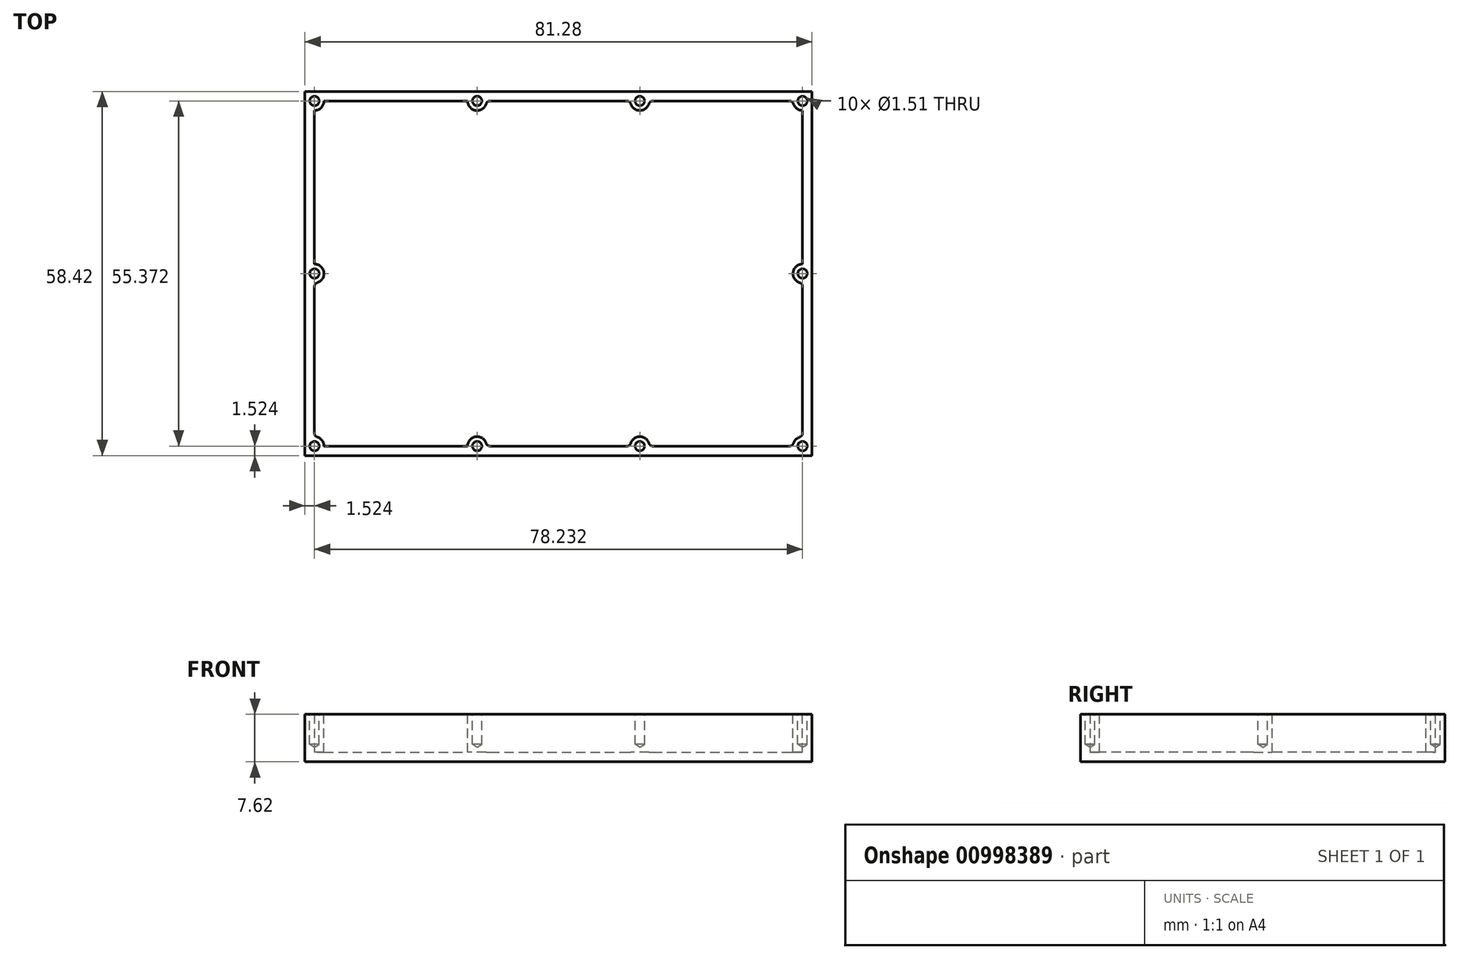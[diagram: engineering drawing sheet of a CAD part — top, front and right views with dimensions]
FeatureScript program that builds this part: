
annotation { "Feature Type Name" : "Feature", "Feature Type Description" : "" }
export const myFeature = defineFeature(function(context is Context, id is Id, definition is map)
    precondition{}
    {
        {
            var Q0;
            Q0=qCreatedBy(makeId("Top.planeOp"),FACE);
            var sketch = newSketch(context, id + "F0", { "sketchPlane" : qUnion([Q0])});
            skLineSegment(sketch, "E0.bottom", {"start": v(-40.64, 29.21) * mm, "end": v(40.64, 29.21) * mm});
            skLineSegment(sketch, "E0.top", {"start": v(-40.64, -29.2) * mm, "end": v(40.64, -29.2) * mm});
            skLineSegment(sketch, "E0.left", {"start": v(-40.64, 29.21) * mm, "end": v(-40.64, -29.2) * mm});
            skLineSegment(sketch, "E0.right", {"start": v(40.64, 29.2) * mm, "end": v(40.64, -29.2) * mm});
            skLineSegment(sketch, "E1", {"start": v(-40.64, -29.2) * mm, "end": v(40.64, 29.2) * mm, "construction": true});
            skSolve(sketch);
        }
        {
            var Q0;
            Q0 = qSketchRegion(id + "F0", true);
            extrude(context, id + "F1", {"entities" : qUnion([Q0]), "endBound" : BoundingType.SYMMETRIC, "depth" : 7.62 * mm, "offsetDistance" : 25.4 * mm});
        }
        {
            var Q0;
            Q0=makeQuery(id+"F1.opExtrude","CAP_FACE",FACE,{"disambiguationData":[OSD([sQuery(id+"F0.wireOp",EDGE,"E0.bottom"),sQuery(id+"F0.wireOp",EDGE,"E0.top"),sQuery(id+"F0.wireOp",EDGE,"E0.left"),sQuery(id+"F0.wireOp",EDGE,"E0.right")])],"isStart":false});
            shell(context, id + "F2", {"entities" : qUnion([Q0]), "thickness" : 1.52 * mm});
        }
        {
            var Q0;
            Q0=makeQuery(id+"F1.opExtrude","CAP_FACE",FACE,{"disambiguationData":[OSD([sQuery(id+"F0.wireOp",EDGE,"E0.bottom"),sQuery(id+"F0.wireOp",EDGE,"E0.top"),sQuery(id+"F0.wireOp",EDGE,"E0.left"),sQuery(id+"F0.wireOp",EDGE,"E0.right")])],"isStart":false});
            var sketch = newSketch(context, id + "F3", { "sketchPlane" : qUnion([Q0])});
            skPoint(sketch, "E2", {"position": v(-39.12, 27.69) * mm});
            skPoint(sketch, "E3.1.0.0", {"position": v(-13.04, 27.69) * mm});
            skPoint(sketch, "E3.2.0.0", {"position": v(13.04, 27.69) * mm});
            skPoint(sketch, "E3.3.0.0", {"position": v(39.12, 27.69) * mm});
            skLineSegment(sketch, "E3.direction1", {"start": v(-39.12, 27.69) * mm, "end": v(-13.04, 27.69) * mm, "construction": true});
            skPoint(sketch, "E4.1.0.0", {"position": v(-39.12, 0) * mm});
            skPoint(sketch, "E4.2.0.0", {"position": v(-39.12, -27.69) * mm});
            skLineSegment(sketch, "E4.direction1", {"start": v(-39.12, 27.69) * mm, "end": v(-39.12, 0) * mm, "construction": true});
            skPoint(sketch, "E5.1.0.0", {"position": v(39.12, 0) * mm});
            skPoint(sketch, "E5.2.0.0", {"position": v(39.12, -27.69) * mm});
            skLineSegment(sketch, "E5.direction1", {"start": v(39.12, 27.69) * mm, "end": v(39.12, 0) * mm, "construction": true});
            skPoint(sketch, "E6.1.0.0", {"position": v(-13.04, -27.69) * mm});
            skPoint(sketch, "E6.2.0.0", {"position": v(13.04, -27.69) * mm});
            skLineSegment(sketch, "E6.direction1", {"start": v(-39.12, -27.69) * mm, "end": v(-13.04, -27.69) * mm, "construction": true});
            skCircle(sketch, "E7", {"center": v(-39.12, 27.69) * mm, "radius": 1.52 * mm});
            skCircle(sketch, "E8", {"center": v(-13.04, 27.69) * mm, "radius": 1.52 * mm});
            skCircle(sketch, "E9", {"center": v(13.04, 27.69) * mm, "radius": 1.52 * mm});
            skCircle(sketch, "E10", {"center": v(39.12, 27.69) * mm, "radius": 1.52 * mm});
            skCircle(sketch, "E11", {"center": v(39.12, 0) * mm, "radius": 1.52 * mm});
            skCircle(sketch, "E12", {"center": v(-39.12, 0) * mm, "radius": 1.52 * mm});
            skCircle(sketch, "E13", {"center": v(-39.12, -27.69) * mm, "radius": 1.52 * mm});
            skCircle(sketch, "E14", {"center": v(-13.04, -27.69) * mm, "radius": 1.52 * mm});
            skCircle(sketch, "E15", {"center": v(13.04, -27.69) * mm, "radius": 1.52 * mm});
            skCircle(sketch, "E16", {"center": v(39.12, -27.69) * mm, "radius": 1.52 * mm});
            skSolve(sketch);
        }
        {
            var Q0;
            {var subQ0=sQuery(id+"F3.wireOp",EDGE,"E7");var subQ1=sQuery(id+"F0.wireOp",EDGE,"E0.bottom");var subQ2=makeQuery(id+"F2.opShell","OFFSET_EDGE",EDGE,{"disambiguationData":[OSD([subQ1]),TDD([makeQuery(id+"F1.opExtrude","CAP_EDGE",EDGE,{"disambiguationData":[OSD([subQ1])],"isStart":false})])]});var subQ3=makeQuery(id+"F3.imprint","INTERSECT",VERTEX,{"derivedFrom":[subQ2,subQ0]});Q0=makeQuery(id+"F3.imprint","IMPRINT",FACE,{"disambiguationData":[TD([[makeQuery(id+"F3.imprint","IMPRINT",EDGE,{"disambiguationData":[TD([[subQ3,1.0]])],"derivedFrom":subQ0}),1.0]])]});}
            var Q1;
            {var subQ0=sQuery(id+"F3.wireOp",EDGE,"E8");var subQ1=sQuery(id+"F0.wireOp",EDGE,"E0.bottom");var subQ2=makeQuery(id+"F2.opShell","OFFSET_EDGE",EDGE,{"disambiguationData":[OSD([subQ1]),TDD([makeQuery(id+"F1.opExtrude","CAP_EDGE",EDGE,{"disambiguationData":[OSD([subQ1])],"isStart":false})])]});var subQ3=makeQuery(id+"F3.imprint","INTERSECT",VERTEX,{"disambiguationData":[OD(0.0)],"derivedFrom":[subQ2,subQ0]});Q1=makeQuery(id+"F3.imprint","IMPRINT",FACE,{"disambiguationData":[TD([[makeQuery(id+"F3.imprint","IMPRINT",EDGE,{"disambiguationData":[TD([[subQ3,1.0]])],"derivedFrom":subQ0}),1.0]])]});}
            var Q2;
            {var subQ0=sQuery(id+"F3.wireOp",EDGE,"E9");var subQ1=sQuery(id+"F0.wireOp",EDGE,"E0.bottom");var subQ2=makeQuery(id+"F2.opShell","OFFSET_EDGE",EDGE,{"disambiguationData":[OSD([subQ1]),TDD([makeQuery(id+"F1.opExtrude","CAP_EDGE",EDGE,{"disambiguationData":[OSD([subQ1])],"isStart":false})])]});var subQ3=makeQuery(id+"F3.imprint","INTERSECT",VERTEX,{"disambiguationData":[OD(0.0)],"derivedFrom":[subQ2,subQ0]});Q2=makeQuery(id+"F3.imprint","IMPRINT",FACE,{"disambiguationData":[TD([[makeQuery(id+"F3.imprint","IMPRINT",EDGE,{"disambiguationData":[TD([[subQ3,1.0]])],"derivedFrom":subQ0}),1.0]])]});}
            var Q3;
            {var subQ0=sQuery(id+"F3.wireOp",EDGE,"E10");var subQ1=sQuery(id+"F0.wireOp",EDGE,"E0.bottom");var subQ2=makeQuery(id+"F2.opShell","OFFSET_EDGE",EDGE,{"disambiguationData":[OSD([subQ1]),TDD([makeQuery(id+"F1.opExtrude","CAP_EDGE",EDGE,{"disambiguationData":[OSD([subQ1])],"isStart":false})])]});var subQ3=makeQuery(id+"F3.imprint","INTERSECT",VERTEX,{"derivedFrom":[subQ2,subQ0]});Q3=makeQuery(id+"F3.imprint","IMPRINT",FACE,{"disambiguationData":[TD([[makeQuery(id+"F3.imprint","IMPRINT",EDGE,{"disambiguationData":[TD([[subQ3,-1.0]])],"derivedFrom":subQ0}),1.0]])]});}
            var Q4;
            {var subQ0=sQuery(id+"F3.wireOp",EDGE,"E11");var subQ1=sQuery(id+"F0.wireOp",EDGE,"E0.right");var subQ2=makeQuery(id+"F2.opShell","OFFSET_EDGE",EDGE,{"disambiguationData":[OSD([subQ1]),TDD([makeQuery(id+"F1.opExtrude","CAP_EDGE",EDGE,{"disambiguationData":[OSD([subQ1])],"isStart":false})])]});var subQ3=makeQuery(id+"F3.imprint","INTERSECT",VERTEX,{"disambiguationData":[OD(0.0)],"derivedFrom":[subQ2,subQ0]});Q4=makeQuery(id+"F3.imprint","IMPRINT",FACE,{"disambiguationData":[TD([[makeQuery(id+"F3.imprint","IMPRINT",EDGE,{"disambiguationData":[TD([[subQ3,-1.0]])],"derivedFrom":subQ0}),1.0]])]});}
            var Q5;
            {var subQ0=sQuery(id+"F3.wireOp",EDGE,"E16");var subQ1=sQuery(id+"F0.wireOp",EDGE,"E0.right");var subQ2=makeQuery(id+"F2.opShell","OFFSET_EDGE",EDGE,{"disambiguationData":[OSD([subQ1]),TDD([makeQuery(id+"F1.opExtrude","CAP_EDGE",EDGE,{"disambiguationData":[OSD([subQ1])],"isStart":false})])]});var subQ3=makeQuery(id+"F3.imprint","INTERSECT",VERTEX,{"derivedFrom":[subQ2,subQ0]});Q5=makeQuery(id+"F3.imprint","IMPRINT",FACE,{"disambiguationData":[TD([[makeQuery(id+"F3.imprint","IMPRINT",EDGE,{"disambiguationData":[TD([[subQ3,-1.0]])],"derivedFrom":subQ0}),1.0]])]});}
            var Q6;
            {var subQ0=sQuery(id+"F3.wireOp",EDGE,"E15");var subQ1=sQuery(id+"F0.wireOp",EDGE,"E0.top");var subQ2=makeQuery(id+"F2.opShell","OFFSET_EDGE",EDGE,{"disambiguationData":[OSD([subQ1]),TDD([makeQuery(id+"F1.opExtrude","CAP_EDGE",EDGE,{"disambiguationData":[OSD([subQ1])],"isStart":false})])]});var subQ3=makeQuery(id+"F3.imprint","INTERSECT",VERTEX,{"disambiguationData":[OD(0.0)],"derivedFrom":[subQ2,subQ0]});Q6=makeQuery(id+"F3.imprint","IMPRINT",FACE,{"disambiguationData":[TD([[makeQuery(id+"F3.imprint","IMPRINT",EDGE,{"disambiguationData":[TD([[subQ3,1.0]])],"derivedFrom":subQ0}),1.0]])]});}
            var Q7;
            {var subQ0=sQuery(id+"F3.wireOp",EDGE,"E14");var subQ1=sQuery(id+"F0.wireOp",EDGE,"E0.top");var subQ2=makeQuery(id+"F2.opShell","OFFSET_EDGE",EDGE,{"disambiguationData":[OSD([subQ1]),TDD([makeQuery(id+"F1.opExtrude","CAP_EDGE",EDGE,{"disambiguationData":[OSD([subQ1])],"isStart":false})])]});var subQ3=makeQuery(id+"F3.imprint","INTERSECT",VERTEX,{"disambiguationData":[OD(0.0)],"derivedFrom":[subQ2,subQ0]});Q7=makeQuery(id+"F3.imprint","IMPRINT",FACE,{"disambiguationData":[TD([[makeQuery(id+"F3.imprint","IMPRINT",EDGE,{"disambiguationData":[TD([[subQ3,1.0]])],"derivedFrom":subQ0}),1.0]])]});}
            var Q8;
            {var subQ0=sQuery(id+"F3.wireOp",EDGE,"E13");var subQ1=sQuery(id+"F0.wireOp",EDGE,"E0.left");var subQ2=makeQuery(id+"F2.opShell","OFFSET_EDGE",EDGE,{"disambiguationData":[OSD([subQ1]),TDD([makeQuery(id+"F1.opExtrude","CAP_EDGE",EDGE,{"disambiguationData":[OSD([subQ1])],"isStart":false})])]});var subQ3=makeQuery(id+"F3.imprint","INTERSECT",VERTEX,{"derivedFrom":[subQ2,subQ0]});Q8=makeQuery(id+"F3.imprint","IMPRINT",FACE,{"disambiguationData":[TD([[makeQuery(id+"F3.imprint","IMPRINT",EDGE,{"disambiguationData":[TD([[subQ3,1.0]])],"derivedFrom":subQ0}),1.0]])]});}
            var Q9;
            {var subQ0=sQuery(id+"F3.wireOp",EDGE,"E12");var subQ1=sQuery(id+"F0.wireOp",EDGE,"E0.left");var subQ2=makeQuery(id+"F2.opShell","OFFSET_EDGE",EDGE,{"disambiguationData":[OSD([subQ1]),TDD([makeQuery(id+"F1.opExtrude","CAP_EDGE",EDGE,{"disambiguationData":[OSD([subQ1])],"isStart":false})])]});var subQ3=makeQuery(id+"F3.imprint","INTERSECT",VERTEX,{"disambiguationData":[OD(0.0)],"derivedFrom":[subQ2,subQ0]});Q9=makeQuery(id+"F3.imprint","IMPRINT",FACE,{"disambiguationData":[TD([[makeQuery(id+"F3.imprint","IMPRINT",EDGE,{"disambiguationData":[TD([[subQ3,1.0]])],"derivedFrom":subQ0}),1.0]])]});}
            var Q10;
            Q10=sQuery(id+"F3.wireOp",EDGE,"E7");
            extrude(context, id + "F4", {"entities" : qUnion([Q0, Q1, Q2, Q3, Q4, Q5, Q6, Q7, Q8, Q9]), "operationType" : NewBodyOperationType.ADD, "surfaceOperationType" : NewSurfaceOperationType.ADD, "surfaceEntities" : qUnion([Q10]), "endBound" : BoundingType.UP_TO_NEXT, "oppositeDirection" : true, "depth" : 7.62 * mm, "offsetDistance" : 25.4 * mm});
        }
        {
            var Q0;
            {var subQ0=sQuery(id+"F0.wireOp",EDGE,"E0.right");var subQ1=sQuery(id+"F0.wireOp",EDGE,"E0.top");var subQ2=sQuery(id+"F0.wireOp",EDGE,"E0.left");var subQ3=sQuery(id+"F0.wireOp",EDGE,"E0.bottom");Q0=makeQuery(id+"F4.boolean.opBoolean","MERGE",FACE,{"derivedFrom":[makeQuery(id+"F1.opExtrude","CAP_FACE",FACE,{"disambiguationData":[OSD([subQ3,subQ1,subQ2,subQ0])],"isStart":false}),makeQuery(id+"F4.opExtrude","CAP_FACE",FACE,{"disambiguationData":[OSD([subQ3,subQ2,sQuery(id+"F3.wireOp",EDGE,"E7")])],"isStart":true}),makeQuery(id+"F4.opExtrude","CAP_FACE",FACE,{"disambiguationData":[OSD([subQ3,sQuery(id+"F3.wireOp",EDGE,"E8")])],"isStart":true}),makeQuery(id+"F4.opExtrude","CAP_FACE",FACE,{"disambiguationData":[OSD([subQ3,sQuery(id+"F3.wireOp",EDGE,"E9")])],"isStart":true}),makeQuery(id+"F4.opExtrude","CAP_FACE",FACE,{"disambiguationData":[OSD([subQ3,subQ0,sQuery(id+"F3.wireOp",EDGE,"E10")])],"isStart":true}),makeQuery(id+"F4.opExtrude","CAP_FACE",FACE,{"disambiguationData":[OSD([subQ0,sQuery(id+"F3.wireOp",EDGE,"E11")])],"isStart":true}),makeQuery(id+"F4.opExtrude","CAP_FACE",FACE,{"disambiguationData":[OSD([subQ2,sQuery(id+"F3.wireOp",EDGE,"E12")])],"isStart":true}),makeQuery(id+"F4.opExtrude","CAP_FACE",FACE,{"disambiguationData":[OSD([subQ1,subQ2,sQuery(id+"F3.wireOp",EDGE,"E13")])],"isStart":true}),makeQuery(id+"F4.opExtrude","CAP_FACE",FACE,{"disambiguationData":[OSD([subQ1,sQuery(id+"F3.wireOp",EDGE,"E14")])],"isStart":true}),makeQuery(id+"F4.opExtrude","CAP_FACE",FACE,{"disambiguationData":[OSD([subQ1,sQuery(id+"F3.wireOp",EDGE,"E15")])],"isStart":true}),makeQuery(id+"F4.opExtrude","CAP_FACE",FACE,{"disambiguationData":[OSD([subQ1,subQ0,sQuery(id+"F3.wireOp",EDGE,"E16")])],"isStart":true})]});}
            var sketch = newSketch(context, id + "F5", { "sketchPlane" : qUnion([Q0])});
            skPoint(sketch, "E17", {"position": v(-39.12, 27.69) * mm});
            skPoint(sketch, "E18.1.0.0", {"position": v(-13.04, 27.69) * mm});
            skPoint(sketch, "E18.2.0.0", {"position": v(13.04, 27.69) * mm});
            skPoint(sketch, "E18.3.0.0", {"position": v(39.12, 27.69) * mm});
            skLineSegment(sketch, "E18.direction1", {"start": v(-39.12, 27.69) * mm, "end": v(-13.04, 27.69) * mm, "construction": true});
            skPoint(sketch, "E19.1.0.0", {"position": v(-39.12, 0) * mm});
            skPoint(sketch, "E19.2.0.0", {"position": v(-39.12, -27.69) * mm});
            skLineSegment(sketch, "E19.direction1", {"start": v(-39.12, 27.69) * mm, "end": v(-39.12, 0) * mm, "construction": true});
            skPoint(sketch, "E20.1.0.0", {"position": v(39.12, 0) * mm});
            skPoint(sketch, "E20.2.0.0", {"position": v(39.12, -27.69) * mm});
            skLineSegment(sketch, "E20.direction1", {"start": v(39.12, 27.69) * mm, "end": v(39.12, 0) * mm, "construction": true});
            skPoint(sketch, "E21.1.0.0", {"position": v(-13.04, -27.69) * mm});
            skPoint(sketch, "E21.2.0.0", {"position": v(13.04, -27.69) * mm});
            skLineSegment(sketch, "E21.direction1", {"start": v(-39.12, -27.69) * mm, "end": v(-13.04, -27.69) * mm, "construction": true});
            skSolve(sketch);
        }
        {
            var Q0;
            Q0=sQuery(id+"F5.wireOp",VERTEX,"E17");
            var Q1;
            Q1=sQuery(id+"F5.wireOp",VERTEX,"E18.1.0.0");
            var Q2;
            Q2=sQuery(id+"F5.wireOp",VERTEX,"E18.2.0.0");
            var Q3;
            Q3=sQuery(id+"F5.wireOp",VERTEX,"E18.3.0.0");
            var Q4;
            Q4=sQuery(id+"F5.wireOp",VERTEX,"E20.1.0.0");
            var Q5;
            Q5=sQuery(id+"F5.wireOp",VERTEX,"E20.2.0.0");
            var Q6;
            Q6=sQuery(id+"F5.wireOp",VERTEX,"E21.2.0.0");
            var Q7;
            Q7=sQuery(id+"F5.wireOp",VERTEX,"E21.1.0.0");
            var Q8;
            Q8=sQuery(id+"F5.wireOp",VERTEX,"E19.2.0.0");
            var Q9;
            Q9=sQuery(id+"F5.wireOp",VERTEX,"E19.1.0.0");
            var Q10;
            Q10=makeQuery(id+"F1.opExtrude","SWEPT_BODY",BODY,{"disambiguationData":[OSD([sQuery(id+"F0.wireOp",EDGE,"E0.bottom"),sQuery(id+"F0.wireOp",EDGE,"E0.top"),sQuery(id+"F0.wireOp",EDGE,"E0.left"),sQuery(id+"F0.wireOp",EDGE,"E0.right")])]});
            hole(context, id + "F6", {"style" : HoleStyle.SIMPLE, "endStyle" : HoleEndStyle.BLIND, "standardTappedOrClearance" : lookupTablePath({ "standard" : "ANSI", "engagement" : "75%", "pitch" : "72 tpi", "size" : "#1", "type" : "Tapped" }), "standardBlindInLast" : lookupTablePath({ "standard" : "ANSI", "fit" : "Normal", "engagement" : "75%", "pitch" : "72 tpi", "size" : "#1", "type" : "Clearance & tapped" }), "holeDiameter" : 1.51 * mm, "majorDiameter" : 1.85 * mm, "showTappedDepth" : true, "holeDepth" : 4.83 * mm, "tappedDepth" : 3.77 * mm, "tapClearance" : 3, "locations" : qUnion([Q0, Q1, Q2, Q3, Q4, Q5, Q6, Q7, Q8, Q9]), "scope" : qUnion([Q10])});
        }
        {
            var Q0;
            Q0=makeQuery(id+"F4.opExtrude","SWEPT_EDGE",EDGE,{"disambiguationData":[OSD([sQuery(id+"F0.wireOp",EDGE,"E0.bottom"),sQuery(id+"F3.wireOp",EDGE,"E7")])]});
            var Q1;
            Q1=makeQuery(id+"F4.opExtrude","SWEPT_EDGE",EDGE,{"disambiguationData":[OSD([sQuery(id+"F0.wireOp",EDGE,"E0.left"),sQuery(id+"F3.wireOp",EDGE,"E7")])]});
            var Q2;
            {var subQ0=sQuery(id+"F3.wireOp",EDGE,"E8");var subQ1=sQuery(id+"F0.wireOp",EDGE,"E0.bottom");Q2=makeQuery(id+"F4.opExtrude","SWEPT_EDGE",EDGE,{"disambiguationData":[OSD([subQ1,subQ0]),TDD([makeQuery(id+"F3.imprint","INTERSECT",VERTEX,{"disambiguationData":[OD(1.0)],"derivedFrom":[makeQuery(id+"F2.opShell","OFFSET_EDGE",EDGE,{"disambiguationData":[OSD([subQ1]),TDD([makeQuery(id+"F1.opExtrude","CAP_EDGE",EDGE,{"disambiguationData":[OSD([subQ1])],"isStart":false})])]}),subQ0]})])]});}
            var Q3;
            {var subQ0=sQuery(id+"F3.wireOp",EDGE,"E8");var subQ1=sQuery(id+"F0.wireOp",EDGE,"E0.bottom");Q3=makeQuery(id+"F4.opExtrude","SWEPT_EDGE",EDGE,{"disambiguationData":[OSD([subQ1,subQ0]),TDD([makeQuery(id+"F3.imprint","INTERSECT",VERTEX,{"disambiguationData":[OD(0.0)],"derivedFrom":[makeQuery(id+"F2.opShell","OFFSET_EDGE",EDGE,{"disambiguationData":[OSD([subQ1]),TDD([makeQuery(id+"F1.opExtrude","CAP_EDGE",EDGE,{"disambiguationData":[OSD([subQ1])],"isStart":false})])]}),subQ0]})])]});}
            var Q4;
            {var subQ0=sQuery(id+"F3.wireOp",EDGE,"E9");var subQ1=sQuery(id+"F0.wireOp",EDGE,"E0.bottom");Q4=makeQuery(id+"F4.opExtrude","SWEPT_EDGE",EDGE,{"disambiguationData":[OSD([subQ1,subQ0]),TDD([makeQuery(id+"F3.imprint","INTERSECT",VERTEX,{"disambiguationData":[OD(1.0)],"derivedFrom":[makeQuery(id+"F2.opShell","OFFSET_EDGE",EDGE,{"disambiguationData":[OSD([subQ1]),TDD([makeQuery(id+"F1.opExtrude","CAP_EDGE",EDGE,{"disambiguationData":[OSD([subQ1])],"isStart":false})])]}),subQ0]})])]});}
            var Q5;
            {var subQ0=sQuery(id+"F3.wireOp",EDGE,"E9");var subQ1=sQuery(id+"F0.wireOp",EDGE,"E0.bottom");Q5=makeQuery(id+"F4.opExtrude","SWEPT_EDGE",EDGE,{"disambiguationData":[OSD([subQ1,subQ0]),TDD([makeQuery(id+"F3.imprint","INTERSECT",VERTEX,{"disambiguationData":[OD(0.0)],"derivedFrom":[makeQuery(id+"F2.opShell","OFFSET_EDGE",EDGE,{"disambiguationData":[OSD([subQ1]),TDD([makeQuery(id+"F1.opExtrude","CAP_EDGE",EDGE,{"disambiguationData":[OSD([subQ1])],"isStart":false})])]}),subQ0]})])]});}
            var Q6;
            Q6=makeQuery(id+"F4.opExtrude","SWEPT_EDGE",EDGE,{"disambiguationData":[OSD([sQuery(id+"F0.wireOp",EDGE,"E0.bottom"),sQuery(id+"F3.wireOp",EDGE,"E10")])]});
            var Q7;
            Q7=makeQuery(id+"F4.opExtrude","SWEPT_EDGE",EDGE,{"disambiguationData":[OSD([sQuery(id+"F0.wireOp",EDGE,"E0.right"),sQuery(id+"F3.wireOp",EDGE,"E10")])]});
            var Q8;
            {var subQ0=sQuery(id+"F3.wireOp",EDGE,"E11");var subQ1=sQuery(id+"F0.wireOp",EDGE,"E0.right");Q8=makeQuery(id+"F4.opExtrude","SWEPT_EDGE",EDGE,{"disambiguationData":[OSD([subQ1,subQ0]),TDD([makeQuery(id+"F3.imprint","INTERSECT",VERTEX,{"disambiguationData":[OD(0.0)],"derivedFrom":[makeQuery(id+"F2.opShell","OFFSET_EDGE",EDGE,{"disambiguationData":[OSD([subQ1]),TDD([makeQuery(id+"F1.opExtrude","CAP_EDGE",EDGE,{"disambiguationData":[OSD([subQ1])],"isStart":false})])]}),subQ0]})])]});}
            var Q9;
            {var subQ0=sQuery(id+"F3.wireOp",EDGE,"E11");var subQ1=sQuery(id+"F0.wireOp",EDGE,"E0.right");Q9=makeQuery(id+"F4.opExtrude","SWEPT_EDGE",EDGE,{"disambiguationData":[OSD([subQ1,subQ0]),TDD([makeQuery(id+"F3.imprint","INTERSECT",VERTEX,{"disambiguationData":[OD(1.0)],"derivedFrom":[makeQuery(id+"F2.opShell","OFFSET_EDGE",EDGE,{"disambiguationData":[OSD([subQ1]),TDD([makeQuery(id+"F1.opExtrude","CAP_EDGE",EDGE,{"disambiguationData":[OSD([subQ1])],"isStart":false})])]}),subQ0]})])]});}
            var Q10;
            Q10=makeQuery(id+"F4.opExtrude","SWEPT_EDGE",EDGE,{"disambiguationData":[OSD([sQuery(id+"F0.wireOp",EDGE,"E0.right"),sQuery(id+"F3.wireOp",EDGE,"E16")])]});
            var Q11;
            Q11=makeQuery(id+"F4.opExtrude","SWEPT_EDGE",EDGE,{"disambiguationData":[OSD([sQuery(id+"F0.wireOp",EDGE,"E0.top"),sQuery(id+"F3.wireOp",EDGE,"E16")])]});
            var Q12;
            {var subQ0=sQuery(id+"F3.wireOp",EDGE,"E15");var subQ1=sQuery(id+"F0.wireOp",EDGE,"E0.top");Q12=makeQuery(id+"F4.opExtrude","SWEPT_EDGE",EDGE,{"disambiguationData":[OSD([subQ1,subQ0]),TDD([makeQuery(id+"F3.imprint","INTERSECT",VERTEX,{"disambiguationData":[OD(1.0)],"derivedFrom":[makeQuery(id+"F2.opShell","OFFSET_EDGE",EDGE,{"disambiguationData":[OSD([subQ1]),TDD([makeQuery(id+"F1.opExtrude","CAP_EDGE",EDGE,{"disambiguationData":[OSD([subQ1])],"isStart":false})])]}),subQ0]})])]});}
            var Q13;
            {var subQ0=sQuery(id+"F3.wireOp",EDGE,"E15");var subQ1=sQuery(id+"F0.wireOp",EDGE,"E0.top");Q13=makeQuery(id+"F4.opExtrude","SWEPT_EDGE",EDGE,{"disambiguationData":[OSD([subQ1,subQ0]),TDD([makeQuery(id+"F3.imprint","INTERSECT",VERTEX,{"disambiguationData":[OD(0.0)],"derivedFrom":[makeQuery(id+"F2.opShell","OFFSET_EDGE",EDGE,{"disambiguationData":[OSD([subQ1]),TDD([makeQuery(id+"F1.opExtrude","CAP_EDGE",EDGE,{"disambiguationData":[OSD([subQ1])],"isStart":false})])]}),subQ0]})])]});}
            var Q14;
            {var subQ0=sQuery(id+"F3.wireOp",EDGE,"E14");var subQ1=sQuery(id+"F0.wireOp",EDGE,"E0.top");Q14=makeQuery(id+"F4.opExtrude","SWEPT_EDGE",EDGE,{"disambiguationData":[OSD([subQ1,subQ0]),TDD([makeQuery(id+"F3.imprint","INTERSECT",VERTEX,{"disambiguationData":[OD(1.0)],"derivedFrom":[makeQuery(id+"F2.opShell","OFFSET_EDGE",EDGE,{"disambiguationData":[OSD([subQ1]),TDD([makeQuery(id+"F1.opExtrude","CAP_EDGE",EDGE,{"disambiguationData":[OSD([subQ1])],"isStart":false})])]}),subQ0]})])]});}
            var Q15;
            {var subQ0=sQuery(id+"F3.wireOp",EDGE,"E14");var subQ1=sQuery(id+"F0.wireOp",EDGE,"E0.top");Q15=makeQuery(id+"F4.opExtrude","SWEPT_EDGE",EDGE,{"disambiguationData":[OSD([subQ1,subQ0]),TDD([makeQuery(id+"F3.imprint","INTERSECT",VERTEX,{"disambiguationData":[OD(0.0)],"derivedFrom":[makeQuery(id+"F2.opShell","OFFSET_EDGE",EDGE,{"disambiguationData":[OSD([subQ1]),TDD([makeQuery(id+"F1.opExtrude","CAP_EDGE",EDGE,{"disambiguationData":[OSD([subQ1])],"isStart":false})])]}),subQ0]})])]});}
            var Q16;
            Q16=makeQuery(id+"F4.opExtrude","SWEPT_EDGE",EDGE,{"disambiguationData":[OSD([sQuery(id+"F0.wireOp",EDGE,"E0.top"),sQuery(id+"F3.wireOp",EDGE,"E13")])]});
            var Q17;
            Q17=makeQuery(id+"F4.opExtrude","SWEPT_EDGE",EDGE,{"disambiguationData":[OSD([sQuery(id+"F0.wireOp",EDGE,"E0.left"),sQuery(id+"F3.wireOp",EDGE,"E13")])]});
            var Q18;
            {var subQ0=sQuery(id+"F3.wireOp",EDGE,"E12");var subQ1=sQuery(id+"F0.wireOp",EDGE,"E0.left");Q18=makeQuery(id+"F4.opExtrude","SWEPT_EDGE",EDGE,{"disambiguationData":[OSD([subQ1,subQ0]),TDD([makeQuery(id+"F3.imprint","INTERSECT",VERTEX,{"disambiguationData":[OD(0.0)],"derivedFrom":[makeQuery(id+"F2.opShell","OFFSET_EDGE",EDGE,{"disambiguationData":[OSD([subQ1]),TDD([makeQuery(id+"F1.opExtrude","CAP_EDGE",EDGE,{"disambiguationData":[OSD([subQ1])],"isStart":false})])]}),subQ0]})])]});}
            var Q19;
            {var subQ0=sQuery(id+"F3.wireOp",EDGE,"E12");var subQ1=sQuery(id+"F0.wireOp",EDGE,"E0.left");Q19=makeQuery(id+"F4.opExtrude","SWEPT_EDGE",EDGE,{"disambiguationData":[OSD([subQ1,subQ0]),TDD([makeQuery(id+"F3.imprint","INTERSECT",VERTEX,{"disambiguationData":[OD(1.0)],"derivedFrom":[makeQuery(id+"F2.opShell","OFFSET_EDGE",EDGE,{"disambiguationData":[OSD([subQ1]),TDD([makeQuery(id+"F1.opExtrude","CAP_EDGE",EDGE,{"disambiguationData":[OSD([subQ1])],"isStart":false})])]}),subQ0]})])]});}
            fillet(context, id + "F7", {"entities" : qUnion([Q0, Q1, Q2, Q3, Q4, Q5, Q6, Q7, Q8, Q9, Q10, Q11, Q12, Q13, Q14, Q15, Q16, Q17, Q18, Q19]), "radius" : 0.64 * mm, "tangentPropagation" : true, "allowEdgeOverflow" : false});
        }
    });
